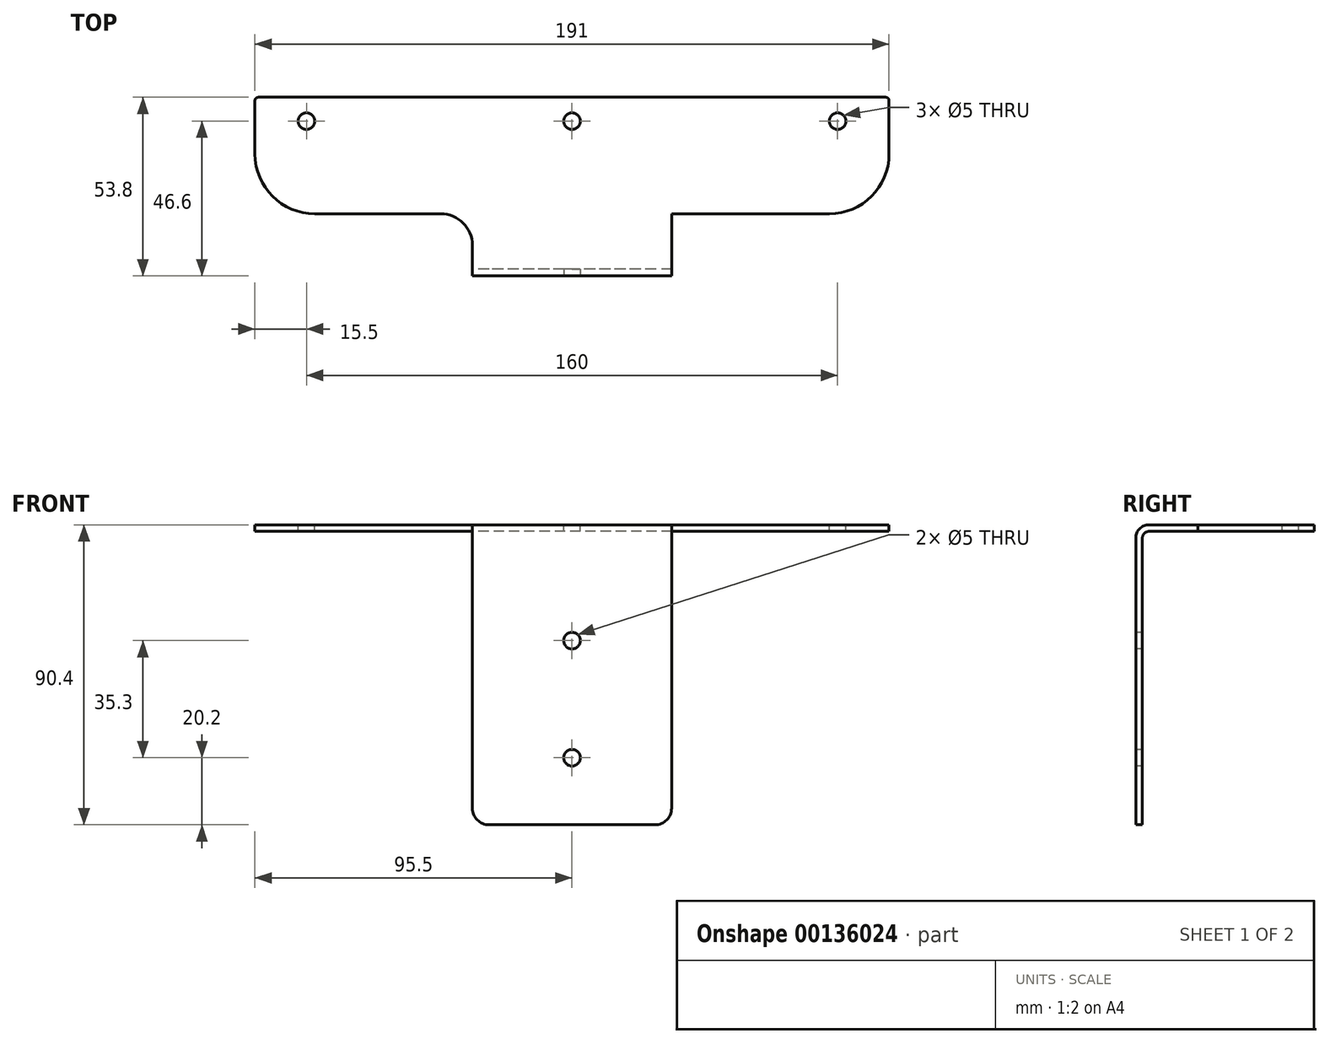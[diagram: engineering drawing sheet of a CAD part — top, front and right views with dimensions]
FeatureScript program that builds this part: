
annotation { "Feature Type Name" : "Feature", "Feature Type Description" : "" }
export const myFeature = defineFeature(function(context is Context, id is Id, definition is map)
    precondition{}
    {
        {
            var Q0;
            Q0=qCreatedBy(makeId("Right.planeOp"),FACE);
            var sketch = newSketch(context, id + "F0", { "sketchPlane" : qUnion([Q0])});
            skLineSegment(sketch, "E0", {"start": v(3.5, 0) * mm, "end": v(53.8, 0) * mm});
            skLineSegment(sketch, "E1", {"start": v(0, -3.5) * mm, "end": v(0, -90.4) * mm});
            skPoint(sketch, "E2.visualSharp", {"position": v(0, 0) * mm});
            skLineSegment(sketch, "E3.0", {"start": v(3.5, -2) * mm, "end": v(53.8, -2) * mm});
            skLineSegment(sketch, "E3.2", {"start": v(2, -3.5) * mm, "end": v(2, -90.4) * mm});
            skLineSegment(sketch, "E4", {"start": v(53.8, 0) * mm, "end": v(53.8, -2) * mm});
            skLineSegment(sketch, "E5", {"start": v(18.7, 0) * mm, "end": v(18.7, -2) * mm, "construction": true});
            skLineSegment(sketch, "E6", {"start": v(18.7, 0) * mm, "end": v(18.7, -2) * mm});
            skLineSegment(sketch, "E7", {"start": v(0, -90.4) * mm, "end": v(2, -90.4) * mm});
            skLineSegment(sketch, "E8", {"start": v(0, -3.5) * mm, "end": v(0, 0) * mm});
            skLineSegment(sketch, "E9", {"start": v(3.5, 0) * mm, "end": v(0, 0) * mm});
            skLineSegment(sketch, "E10", {"start": v(2, -3.5) * mm, "end": v(2, -2) * mm});
            skLineSegment(sketch, "E11", {"start": v(2, -2) * mm, "end": v(3.5, -2) * mm});
            skSolve(sketch);
        }
        {
            var Q0;
            {var subQ0=sQuery(id+"F0.wireOp",EDGE,"E4");Q0=makeQuery(id+"F0.imprint","IMPRINT",FACE,{"disambiguationData":[TD([[makeQuery(id+"F0.imprint","IMPRINT",EDGE,{"derivedFrom":subQ0}),-1.0]])]});}
            extrude(context, id + "F1", {"entities" : qUnion([Q0]), "endBound" : BoundingType.SYMMETRIC, "depth" : 191 * mm});
        }
        {
            var Q0;
            Q0=makeQuery(id+"F0.imprint","IMPRINT",FACE,{"disambiguationData":[TD([[makeQuery(id+"F0.imprint","IMPRINT",EDGE,{"derivedFrom":sQuery(id+"F0.wireOp",EDGE,"E1")}),1.0]])]});
            extrude(context, id + "F2", {"entities" : qUnion([Q0]), "operationType" : NewBodyOperationType.ADD, "endBound" : BoundingType.SYMMETRIC, "depth" : 60 * mm});
        }
        {
            var Q0;
            Q0=makeQuery(id+"F1.opExtrude","CAP_EDGE",EDGE,{"disambiguationData":[OSD([sQuery(id+"F0.wireOp",EDGE,"E6")])],"isStart":false});
            var Q1;
            Q1=makeQuery(id+"F1.opExtrude","CAP_EDGE",EDGE,{"disambiguationData":[OSD([sQuery(id+"F0.wireOp",EDGE,"E6")])],"isStart":true});
            fillet(context, id + "F3", {"entities" : qUnion([Q0, Q1]), "radius" : 18 * mm, "tangentPropagation" : true, "allowEdgeOverflow" : false});
        }
        {
            var Q0;
            Q0=makeQuery(id+"F2.opExtrude","CAP_EDGE",EDGE,{"disambiguationData":[OSD([sQuery(id+"F0.wireOp",EDGE,"E6")])],"isStart":true});
            var Q1;
            Q1=makeQuery(id+"F2.opExtrude","CAP_EDGE",EDGE,{"disambiguationData":[OSD([sQuery(id+"F0.wireOp",EDGE,"E6")])],"isStart":false});
            fillet(context, id + "F4", {"entities" : qUnion([Q0, Q1]), "radius" : 9.5 * mm, "tangentPropagation" : true, "allowEdgeOverflow" : false});
        }
        {
            var Q0;
            Q0=makeQuery(id+"F2.opExtrude","CAP_EDGE",EDGE,{"disambiguationData":[OSD([sQuery(id+"F0.wireOp",EDGE,"E7")])],"isStart":true});
            var Q1;
            Q1=makeQuery(id+"F2.opExtrude","CAP_EDGE",EDGE,{"disambiguationData":[OSD([sQuery(id+"F0.wireOp",EDGE,"E7")])],"isStart":false});
            fillet(context, id + "F5", {"entities" : qUnion([Q0, Q1]), "radius" : 5 * mm, "tangentPropagation" : true, "allowEdgeOverflow" : false});
        }
        {
            var Q0;
            Q0=makeQuery(id+"F2.opExtrude","SWEPT_FACE",FACE,{"disambiguationData":[OSD([sQuery(id+"F0.wireOp",EDGE,"E1")])]});
            var sketch = newSketch(context, id + "F6", { "sketchPlane" : qUnion([Q0])});
            skCircle(sketch, "E12", {"center": v(0, -70.2) * mm, "radius": 2.5 * mm});
            skCircle(sketch, "E13", {"center": v(0, -34.9) * mm, "radius": 2.5 * mm});
            skSolve(sketch);
        }
        {
            var Q0;
            Q0=sQuery(id+"F6.wireOp",VERTEX,"E12.center");
            var Q1;
            Q1=sQuery(id+"F6.wireOp",VERTEX,"E13.center");
            var Q2;
            Q2=makeQuery(id+"F1.opExtrude","SWEPT_BODY",BODY,{"disambiguationData":[OSD([sQuery(id+"F0.wireOp",EDGE,"E0"),sQuery(id+"F0.wireOp",EDGE,"E3.0"),sQuery(id+"F0.wireOp",EDGE,"E4"),sQuery(id+"F0.wireOp",EDGE,"E6")])]});
            hole(context, id + "F7", {"style" : HoleStyle.SIMPLE, "endStyle" : HoleEndStyle.THROUGH, "holeDiameter" : 5 * mm, "locations" : qUnion([Q0, Q1]), "scope" : qUnion([Q2]), "isTappedThrough" : true});
        }
        {
            var Q0;
            {var subQ0=sQuery(id+"F0.wireOp",EDGE,"E0");Q0=makeQuery(id+"F2.boolean.opBoolean","MERGE",FACE,{"derivedFrom":[makeQuery(id+"F1.opExtrude","SWEPT_FACE",FACE,{"disambiguationData":[OSD([subQ0])]}),makeQuery(id+"F2.opExtrude","SWEPT_FACE",FACE,{"disambiguationData":[OSD([subQ0])]})]});}
            var sketch = newSketch(context, id + "F8", { "sketchPlane" : qUnion([Q0])});
            skLineSegment(sketch, "E14", {"start": v(-109.44, 46.6) * mm, "end": v(107.09, 46.6) * mm, "construction": true});
            skCircle(sketch, "E15", {"center": v(0, 46.6) * mm, "radius": 2.25 * mm});
            skCircle(sketch, "E16", {"center": v(-80, 46.6) * mm, "radius": 2.25 * mm});
            skCircle(sketch, "E17.MirrorC", {"center": v(80, 46.6) * mm, "radius": 2.25 * mm});
            skSolve(sketch);
        }
        {
            var Q0;
            Q0=sQuery(id+"F8.wireOp",VERTEX,"E16.center");
            var Q1;
            Q1=sQuery(id+"F8.wireOp",VERTEX,"E15.center");
            var Q2;
            Q2=sQuery(id+"F8.wireOp",VERTEX,"E17.MirrorC.center");
            var Q3;
            Q3=makeQuery(id+"F1.opExtrude","SWEPT_BODY",BODY,{"disambiguationData":[OSD([sQuery(id+"F0.wireOp",EDGE,"E0"),sQuery(id+"F0.wireOp",EDGE,"E3.0"),sQuery(id+"F0.wireOp",EDGE,"E4"),sQuery(id+"F0.wireOp",EDGE,"E6")])]});
            hole(context, id + "F9", {"style" : HoleStyle.SIMPLE, "endStyle" : HoleEndStyle.THROUGH, "holeDiameter" : 5 * mm, "locations" : qUnion([Q0, Q1, Q2]), "scope" : qUnion([Q3]), "isTappedThrough" : true});
        }
        {
            var Q0;
            Q0=makeQuery(id+"F1.opExtrude","CAP_EDGE",EDGE,{"disambiguationData":[OSD([sQuery(id+"F0.wireOp",EDGE,"E4")])],"isStart":false});
            var Q1;
            Q1=makeQuery(id+"F1.opExtrude","CAP_EDGE",EDGE,{"disambiguationData":[OSD([sQuery(id+"F0.wireOp",EDGE,"E4")])],"isStart":true});
            fillet(context, id + "F10", {"entities" : qUnion([Q0, Q1]), "radius" : 1 * mm, "tangentPropagation" : true, "allowEdgeOverflow" : false});
        }
        {
            var Q0;
            Q0=makeQuery(id+"F2.opExtrude","SWEPT_EDGE",EDGE,{"disambiguationData":[OSD([sQuery(id+"F0.wireOp",EDGE,"E8"),sQuery(id+"F0.wireOp",EDGE,"E9")])]});
            fillet(context, id + "F11", {"entities" : qUnion([Q0]), "radius" : 4 * mm, "tangentPropagation" : true, "allowEdgeOverflow" : false});
        }
        {
            var Q0;
            Q0=makeQuery(id+"F2.opExtrude","SWEPT_EDGE",EDGE,{"disambiguationData":[OSD([sQuery(id+"F0.wireOp",EDGE,"E10"),sQuery(id+"F0.wireOp",EDGE,"E11")])]});
            fillet(context, id + "F12", {"entities" : qUnion([Q0]), "radius" : 2 * mm, "tangentPropagation" : true, "allowEdgeOverflow" : false});
        }
    });
